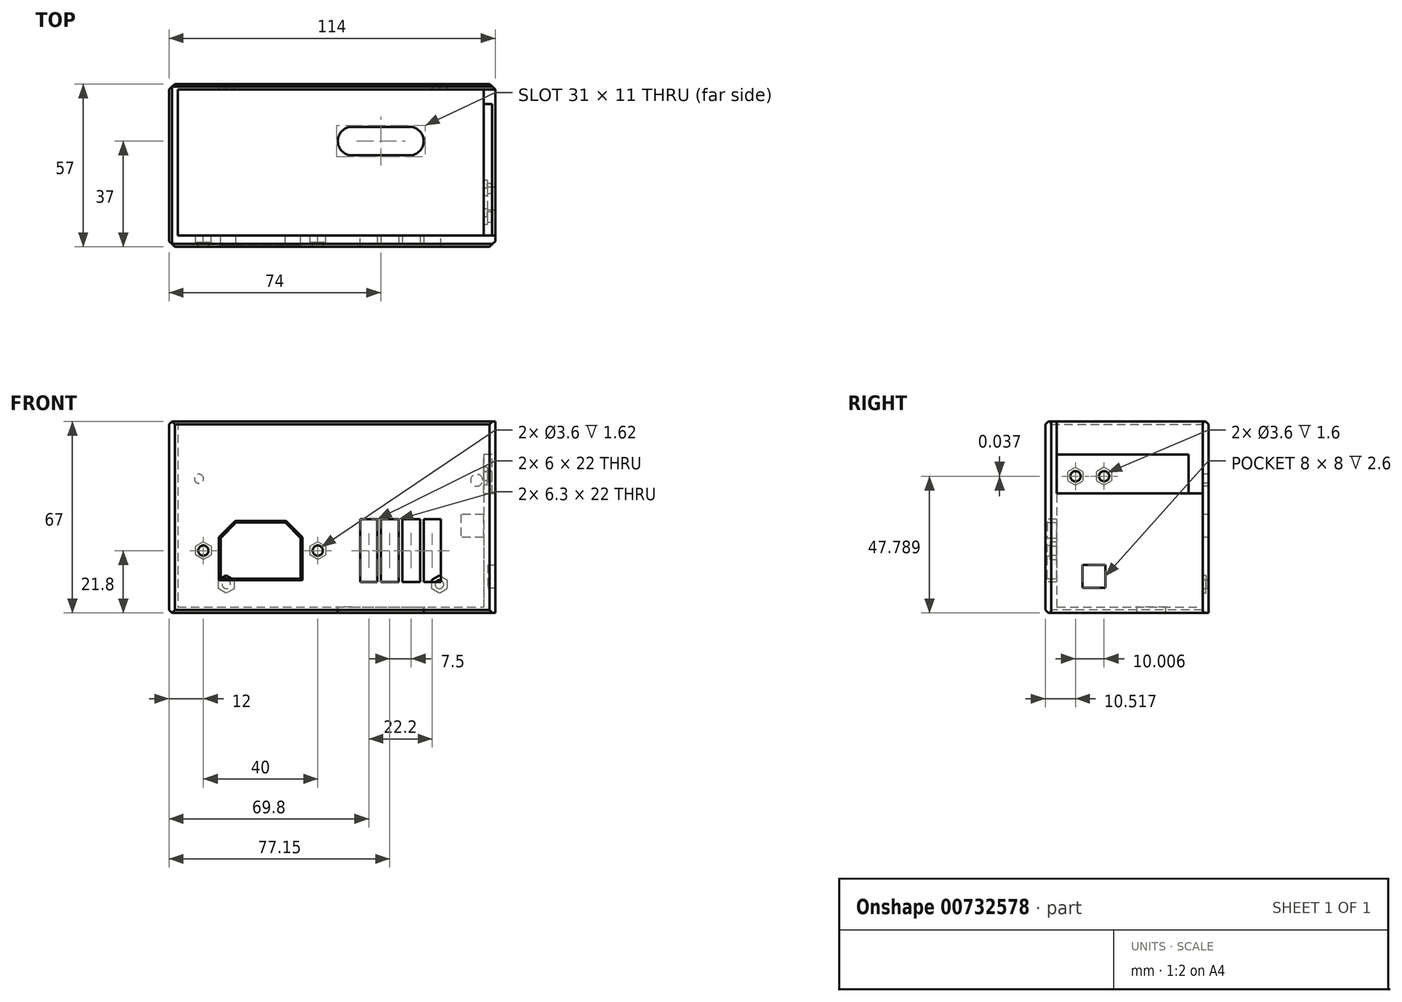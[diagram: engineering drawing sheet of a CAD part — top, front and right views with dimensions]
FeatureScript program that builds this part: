
annotation { "Feature Type Name" : "Feature", "Feature Type Description" : "" }
export const myFeature = defineFeature(function(context is Context, id is Id, definition is map)
    precondition{}
    {
        {
            var Q0;
            Q0=qCreatedBy(makeId("Front.planeOp"),FACE);
            cPlane(context, id + "F0", {"entities" : qUnion([Q0]), "cplaneType" : CPlaneType.OFFSET, "offset" : 2 * mm, "width" : 150 * mm, "height" : 150 * mm});
        }
        {
            var Q0;
            Q0=qCreatedBy(id+"F0.planeOp",FACE);
            var sketch = newSketch(context, id + "F1", { "sketchPlane" : qUnion([Q0])});
            skLineSegment(sketch, "E0.bottom", {"start": v(-111, 105) * mm, "end": v(0, 105) * mm});
            skLineSegment(sketch, "E0.top", {"start": v(-111, 40) * mm, "end": v(0, 40) * mm});
            skLineSegment(sketch, "E0.left", {"start": v(-111, 105) * mm, "end": v(-111, 40) * mm});
            skLineSegment(sketch, "E0.right", {"start": v(0, 105) * mm, "end": v(0, 40) * mm});
            skCircle(sketch, "E1.MirrorC", {"center": v(-93.99, 48.01) * mm, "radius": 1.5 * mm});
            skCircle(sketch, "E2.MirrorC", {"center": v(-19.49, 47.99) * mm, "radius": 1.5 * mm});
            skCircle(sketch, "E3.MirrorC", {"center": v(-6.46, 84.41) * mm, "radius": 2.1 * mm});
            skCircle(sketch, "E4", {"center": v(-103.55, 84.94) * mm, "radius": 1.6 * mm});
            skLineSegment(sketch, "E5.bottom", {"start": v(-4, 72.5) * mm, "end": v(-12, 72.5) * mm});
            skLineSegment(sketch, "E5.top", {"start": v(-4, 64.5) * mm, "end": v(-12, 64.5) * mm});
            skLineSegment(sketch, "E5.left", {"start": v(-4, 72.5) * mm, "end": v(-4, 64.5) * mm});
            skLineSegment(sketch, "E5.right", {"start": v(-12, 72.5) * mm, "end": v(-12, 64.5) * mm});
            skSolve(sketch);
        }
        {
            var Q0;
            Q0=qCreatedBy(id+"F0.planeOp",FACE);
            cPlane(context, id + "F2", {"entities" : qUnion([Q0]), "cplaneType" : CPlaneType.OFFSET, "offset" : 51 * mm, "width" : 150 * mm, "height" : 150 * mm});
        }
        {
            var Q0;
            Q0=qCreatedBy(makeId("Right.planeOp"),FACE);
            cPlane(context, id + "F3", {"entities" : qUnion([Q0]), "cplaneType" : CPlaneType.OFFSET, "offset" : 111 * mm, "oppositeDirection" : true, "width" : 150 * mm, "height" : 150 * mm});
        }
        {
            var Q0;
            Q0=qCreatedBy(makeId("Top.planeOp"),FACE);
            cPlane(context, id + "F4", {"entities" : qUnion([Q0]), "cplaneType" : CPlaneType.OFFSET, "offset" : 40 * mm, "width" : 150 * mm, "height" : 150 * mm});
        }
        {
            var Q0;
            Q0=qCreatedBy(makeId("Right.planeOp"),FACE);
            var sketch = newSketch(context, id + "F5", { "sketchPlane" : qUnion([Q0])});
            skLineSegment(sketch, "E6.bottom", {"start": v(-57, 40) * mm, "end": v(0, 40) * mm});
            skLineSegment(sketch, "E6.top", {"start": v(-57, 93.4) * mm, "end": v(0, 93.4) * mm});
            skLineSegment(sketch, "E6.left", {"start": v(-57, 40) * mm, "end": v(-57, 93.4) * mm});
            skLineSegment(sketch, "E6.right", {"start": v(0, 40) * mm, "end": v(0, 93.4) * mm});
            skCircle(sketch, "E7", {"center": v(-46.48, 85.79) * mm, "radius": 1.8 * mm});
            skCircle(sketch, "E8", {"center": v(-36.48, 85.83) * mm, "radius": 1.8 * mm});
            skLineSegment(sketch, "E9", {"start": v(0, 122) * mm, "end": v(0, -14.27) * mm, "construction": true});
            skSolve(sketch);
        }
        {
            var Q0;
            Q0=qCreatedBy(id+"F4.planeOp",FACE);
            var sketch = newSketch(context, id + "F6", { "sketchPlane" : qUnion([Q0])});
            skLineSegment(sketch, "E10.bottom", {"start": v(0, 0) * mm, "end": v(-114, 0) * mm});
            skLineSegment(sketch, "E10.top", {"start": v(0, -57) * mm, "end": v(-114, -57) * mm});
            skLineSegment(sketch, "E10.left", {"start": v(0, 0) * mm, "end": v(0, -57) * mm});
            skLineSegment(sketch, "E10.right", {"start": v(-114, 0) * mm, "end": v(-114, -57) * mm});
            skLineSegment(sketch, "E11.bottom", {"start": v(-55, -15) * mm, "end": v(-25, -15) * mm});
            skLineSegment(sketch, "E11.top", {"start": v(-55, -25) * mm, "end": v(-25, -25) * mm});
            skLineSegment(sketch, "E11.left", {"start": v(-55, -15) * mm, "end": v(-55, -25) * mm});
            skLineSegment(sketch, "E11.right", {"start": v(-25, -15) * mm, "end": v(-25, -25) * mm});
            skSolve(sketch);
        }
        {
            var Q0;
            Q0=qCreatedBy(id+"F3.planeOp",FACE);
            var sketch = newSketch(context, id + "F7", { "sketchPlane" : qUnion([Q0])});
            skLineSegment(sketch, "E12.0.0", {"start": v(0, 105) * mm, "end": v(-57, 105) * mm});
            skLineSegment(sketch, "E12.0.1", {"start": v(-57, 105) * mm, "end": v(-57, 40) * mm});
            skLineSegment(sketch, "E12.0.2", {"start": v(-57, 40) * mm, "end": v(0, 40) * mm});
            skLineSegment(sketch, "E12.0.3", {"start": v(0, 40) * mm, "end": v(0, 105) * mm});
            skSolve(sketch);
        }
        {
            var Q0;
            Q0=qSketchRegion(id+"F7",true);
            extrude(context, id + "F8", {"entities" : qUnion([Q0]), "oppositeDirection" : true, "depth" : 3 * mm, "offsetDistance" : 25 * mm});
        }
        {
            var Q0;
            Q0=makeQuery(id+"F6.imprint","IMPRINT",FACE,{"disambiguationData":[TD([[makeQuery(id+"F6.imprint","IMPRINT",EDGE,{"derivedFrom":sQuery(id+"F6.wireOp",EDGE,"E10.bottom")}),1.0]])]});
            extrude(context, id + "F9", {"entities" : qUnion([Q0]), "operationType" : NewBodyOperationType.ADD, "oppositeDirection" : true, "depth" : 2 * mm, "offsetDistance" : 25 * mm});
        }
        {
            var Q0;
            Q0=makeQuery(id+"F9.opExtrude","SWEPT_EDGE",EDGE,{"disambiguationData":[OSD([sQuery(id+"F6.wireOp",EDGE,"E11.top"),sQuery(id+"F6.wireOp",EDGE,"E11.right")])]});
            var Q1;
            Q1=makeQuery(id+"F9.opExtrude","SWEPT_EDGE",EDGE,{"disambiguationData":[OSD([sQuery(id+"F6.wireOp",EDGE,"E11.top"),sQuery(id+"F6.wireOp",EDGE,"E11.left")])]});
            var Q2;
            Q2=makeQuery(id+"F9.opExtrude","SWEPT_EDGE",EDGE,{"disambiguationData":[OSD([sQuery(id+"F6.wireOp",EDGE,"E11.bottom"),sQuery(id+"F6.wireOp",EDGE,"E11.left")])]});
            var Q3;
            Q3=makeQuery(id+"F9.opExtrude","SWEPT_EDGE",EDGE,{"disambiguationData":[OSD([sQuery(id+"F6.wireOp",EDGE,"E11.bottom"),sQuery(id+"F6.wireOp",EDGE,"E11.right")])]});
            fillet(context, id + "F10", {"entities" : qUnion([Q0, Q1, Q2, Q3]), "radius" : 5 * mm, "tangentPropagation" : true, "allowEdgeOverflow" : false});
        }
        {
            var Q0;
            Q0=makeQuery(id+"F5.imprint","IMPRINT",FACE,{"disambiguationData":[TD([[makeQuery(id+"F5.imprint","IMPRINT",EDGE,{"derivedFrom":sQuery(id+"F5.wireOp",EDGE,"E6.bottom")}),1.0]])]});
            extrude(context, id + "F11", {"entities" : qUnion([Q0]), "operationType" : NewBodyOperationType.ADD, "oppositeDirection" : true, "depth" : 4 * mm, "offsetDistance" : 25 * mm});
        }
        {
            var Q0;
            Q0=makeQuery(id+"F5.imprint","IMPRINT",FACE,{"disambiguationData":[TD([[makeQuery(id+"F5.imprint","IMPRINT",EDGE,{"derivedFrom":sQuery(id+"F5.wireOp",EDGE,"E6.bottom")}),1.0]])]});
            var sketch = newSketch(context, id + "F12", { "sketchPlane" : qUnion([Q0])});
            skLineSegment(sketch, "E13.bottom", {"start": v(-53, 105) * mm, "end": v(-2, 105) * mm});
            skLineSegment(sketch, "E13.top", {"start": v(-53, 79.75) * mm, "end": v(-2, 79.75) * mm});
            skLineSegment(sketch, "E13.left", {"start": v(-53, 105) * mm, "end": v(-53, 79.75) * mm});
            skLineSegment(sketch, "E13.right", {"start": v(-2, 105) * mm, "end": v(-2, 79.75) * mm});
            skSolve(sketch);
        }
        {
            var Q0;
            Q0=qSketchRegion(id+"F12",true);
            extrude(context, id + "F13", {"entities" : qUnion([Q0]), "operationType" : NewBodyOperationType.REMOVE, "oppositeDirection" : true, "depth" : 1.1 * mm, "offsetDistance" : 25 * mm});
        }
        {
            var Q0;
            Q0=makeQuery(id+"F11.boolean.opBoolean","MERGE",FACE,{"derivedFrom":[makeQuery(id+"F9.opExtrude","SWEPT_FACE",FACE,{"disambiguationData":[OSD([sQuery(id+"F6.wireOp",EDGE,"E10.left")])]}),makeQuery(id+"F11.opExtrude","CAP_FACE",FACE,{"disambiguationData":[OSD([sQuery(id+"F5.wireOp",EDGE,"E6.bottom"),sQuery(id+"F5.wireOp",EDGE,"E6.top"),sQuery(id+"F5.wireOp",EDGE,"E6.left"),sQuery(id+"F5.wireOp",EDGE,"E6.right"),sQuery(id+"F5.wireOp",EDGE,"E7"),sQuery(id+"F5.wireOp",EDGE,"E8")])],"isStart":true})]});
            extrude(context, id + "F14", {"entities" : qUnion([Q0]), "operationType" : NewBodyOperationType.ADD, "oppositeDirection" : true, "depth" : 4 * mm, "offsetDistance" : 25 * mm});
        }
        {
            var Q0;
            Q0=makeQuery(id+"F5.imprint","IMPRINT",FACE,{"disambiguationData":[TD([[makeQuery(id+"F5.imprint","IMPRINT",EDGE,{"derivedFrom":sQuery(id+"F5.wireOp",EDGE,"E6.bottom")}),1.0]])]});
            var sketch = newSketch(context, id + "F15", { "sketchPlane" : qUnion([Q0])});
            skLineSegment(sketch, "E14.bottom", {"start": v(-2, 79.75) * mm, "end": v(-7, 79.75) * mm});
            skLineSegment(sketch, "E14.top", {"start": v(-2, 105) * mm, "end": v(-7, 105) * mm});
            skLineSegment(sketch, "E14.left", {"start": v(-2, 79.75) * mm, "end": v(-2, 105) * mm});
            skLineSegment(sketch, "E14.right", {"start": v(-7, 79.75) * mm, "end": v(-7, 105) * mm});
            skSolve(sketch);
        }
        {
            var Q0;
            Q0=qSketchRegion(id+"F15",true);
            extrude(context, id + "F16", {"entities" : qUnion([Q0]), "operationType" : NewBodyOperationType.REMOVE, "oppositeDirection" : true, "depth" : 4.1 * mm, "offsetDistance" : 25 * mm});
        }
        {
            var Q0;
            Q0=qSketchRegion(id+"F1",true);
            extrude(context, id + "F17", {"entities" : qUnion([Q0]), "operationType" : NewBodyOperationType.ADD, "oppositeDirection" : true, "depth" : 2 * mm, "offsetDistance" : 25 * mm});
        }
        {
            var Q0;
            Q0=qCreatedBy(id+"F2.planeOp",FACE);
            var sketch = newSketch(context, id + "F18", { "sketchPlane" : qUnion([Q0])});
            skLineSegment(sketch, "E15.bottom", {"start": v(-111, 105) * mm, "end": v(0, 105) * mm});
            skLineSegment(sketch, "E15.top", {"start": v(-111, 40) * mm, "end": v(0, 40) * mm});
            skLineSegment(sketch, "E15.left", {"start": v(-111, 105) * mm, "end": v(-111, 40) * mm});
            skLineSegment(sketch, "E15.right", {"start": v(0, 105) * mm, "end": v(0, 40) * mm});
            skLineSegment(sketch, "E16", {"start": v(-90.6, 69.6) * mm, "end": v(-73.4, 69.6) * mm});
            skLineSegment(sketch, "E17", {"start": v(-73.4, 69.6) * mm, "end": v(-68, 64.2) * mm});
            skLineSegment(sketch, "E18", {"start": v(-68, 64.2) * mm, "end": v(-68, 50) * mm});
            skLineSegment(sketch, "E19", {"start": v(-68, 50) * mm, "end": v(-96, 50) * mm});
            skLineSegment(sketch, "E20", {"start": v(-96, 50) * mm, "end": v(-96, 64.2) * mm});
            skLineSegment(sketch, "E21", {"start": v(-96, 64.2) * mm, "end": v(-90.6, 69.6) * mm});
            skLineSegment(sketch, "E22", {"start": v(-82, 69.6) * mm, "end": v(-82, 50) * mm, "construction": true});
            skCircle(sketch, "E23", {"center": v(-62, 59.8) * mm, "radius": 1.8 * mm});
            skLineSegment(sketch, "E24", {"start": v(-82, 59.8) * mm, "end": v(-111, 59.8) * mm, "construction": true});
            skLineSegment(sketch, "E25", {"start": v(-111, 59.8) * mm, "end": v(-6.13, 59.8) * mm, "construction": true});
            skCircle(sketch, "E26", {"center": v(-102, 59.8) * mm, "radius": 1.8 * mm});
            skLineSegment(sketch, "E27.bottom", {"start": v(-47.2, 70.8) * mm, "end": v(-19, 70.8) * mm});
            skLineSegment(sketch, "E27.top", {"start": v(-47.2, 48.8) * mm, "end": v(-19, 48.8) * mm});
            skLineSegment(sketch, "E27.left", {"start": v(-47.2, 70.8) * mm, "end": v(-47.2, 48.8) * mm});
            skLineSegment(sketch, "E27.right", {"start": v(-19, 70.8) * mm, "end": v(-19, 48.8) * mm});
            skSolve(sketch);
        }
        {
            var Q0;
            Q0=makeQuery(id+"F11.boolean.opBoolean","MERGE",EDGE,{"derivedFrom":[makeQuery(id+"F9.opExtrude","SWEPT_EDGE",EDGE,{"disambiguationData":[OSD([sQuery(id+"F6.wireOp",EDGE,"E10.bottom"),sQuery(id+"F6.wireOp",EDGE,"E10.left")])]}),makeQuery(id+"F11.opExtrude","CAP_EDGE",EDGE,{"disambiguationData":[OSD([sQuery(id+"F5.wireOp",EDGE,"E6.right")])],"isStart":true})]});
            chamfer(context, id + "F19", {"entities" : qUnion([Q0]), "width" : 2 * mm, "tangentPropagation" : true});
        }
        {
            var Q0;
            Q0=makeQuery(id+"F9.boolean.opBoolean","MERGE",EDGE,{"derivedFrom":[makeQuery(id+"F8.opExtrude","CAP_EDGE",EDGE,{"disambiguationData":[OSD([sQuery(id+"F7.wireOp",EDGE,"E12.0.3")])],"isStart":false}),makeQuery(id+"F9.opExtrude","SWEPT_EDGE",EDGE,{"disambiguationData":[OSD([sQuery(id+"F6.wireOp",EDGE,"E10.bottom"),sQuery(id+"F6.wireOp",EDGE,"E10.right")])]})]});
            chamfer(context, id + "F20", {"entities" : qUnion([Q0]), "width" : 2 * mm, "tangentPropagation" : true});
        }
        {
            var Q0;
            Q0=makeQuery(id+"F18.imprint","IMPRINT",FACE,{"disambiguationData":[TD([[makeQuery(id+"F18.imprint","IMPRINT",EDGE,{"derivedFrom":sQuery(id+"F18.wireOp",EDGE,"E15.bottom")}),-1.0]])]});
            extrude(context, id + "F21", {"entities" : qUnion([Q0]), "operationType" : NewBodyOperationType.ADD, "depth" : 4 * mm, "offsetDistance" : 25 * mm});
        }
        {
            var Q0;
            Q0=makeQuery(id+"F11.boolean.opBoolean","MERGE",EDGE,{"derivedFrom":[makeQuery(id+"F9.opExtrude","SWEPT_EDGE",EDGE,{"disambiguationData":[OSD([sQuery(id+"F6.wireOp",EDGE,"E10.top"),sQuery(id+"F6.wireOp",EDGE,"E10.left")])]}),makeQuery(id+"F11.opExtrude","CAP_EDGE",EDGE,{"disambiguationData":[OSD([sQuery(id+"F5.wireOp",EDGE,"E6.left")])],"isStart":true})]});
            chamfer(context, id + "F22", {"entities" : qUnion([Q0]), "width" : 2 * mm, "tangentPropagation" : true});
        }
        {
            var Q0;
            Q0=makeQuery(id+"F9.boolean.opBoolean","MERGE",EDGE,{"derivedFrom":[makeQuery(id+"F8.opExtrude","CAP_EDGE",EDGE,{"disambiguationData":[OSD([sQuery(id+"F7.wireOp",EDGE,"E12.0.1")])],"isStart":false}),makeQuery(id+"F9.opExtrude","SWEPT_EDGE",EDGE,{"disambiguationData":[OSD([sQuery(id+"F6.wireOp",EDGE,"E10.top"),sQuery(id+"F6.wireOp",EDGE,"E10.right")])]})]});
            chamfer(context, id + "F23", {"entities" : qUnion([Q0]), "width" : 2 * mm, "tangentPropagation" : true});
        }
        {
            var Q0;
            Q0=makeQuery(id+"F21.boolean.opBoolean","MERGE",EDGE,{"derivedFrom":[makeQuery(id+"F8.opExtrude","SWEPT_EDGE",EDGE,{"disambiguationData":[OSD([sQuery(id+"F7.wireOp",EDGE,"E12.0.0"),sQuery(id+"F7.wireOp",EDGE,"E12.0.1")])]}),makeQuery(id+"F11.opExtrude","SWEPT_EDGE",EDGE,{"disambiguationData":[OSD([sQuery(id+"F5.wireOp",EDGE,"E6.top"),sQuery(id+"F5.wireOp",EDGE,"E6.left")])]}),makeQuery(id+"F21.opExtrude","CAP_EDGE",EDGE,{"disambiguationData":[OSD([sQuery(id+"F18.wireOp",EDGE,"E15.bottom")])],"isStart":false})]});
            var Q1;
            Q1=makeQuery(id+"F17.boolean.opBoolean","MERGE",EDGE,{"derivedFrom":[makeQuery(id+"F8.opExtrude","SWEPT_EDGE",EDGE,{"disambiguationData":[OSD([sQuery(id+"F7.wireOp",EDGE,"E12.0.0"),sQuery(id+"F7.wireOp",EDGE,"E12.0.3")])]}),makeQuery(id+"F11.opExtrude","SWEPT_EDGE",EDGE,{"disambiguationData":[OSD([sQuery(id+"F5.wireOp",EDGE,"E6.top"),sQuery(id+"F5.wireOp",EDGE,"E6.right")])]}),makeQuery(id+"F17.opExtrude","CAP_EDGE",EDGE,{"disambiguationData":[OSD([sQuery(id+"F1.wireOp",EDGE,"E0.bottom")])],"isStart":false})]});
            var Q2;
            Q2=makeQuery(id+"F8.opExtrude","CAP_EDGE",EDGE,{"disambiguationData":[OSD([sQuery(id+"F7.wireOp",EDGE,"E12.0.0")])],"isStart":false});
            chamfer(context, id + "F24", {"entities" : qUnion([Q0, Q1, Q2]), "width" : 1 * mm, "tangentPropagation" : true});
        }
        {
            var Q0;
            Q0=makeQuery(id+"F9.opExtrude","CAP_EDGE",EDGE,{"disambiguationData":[OSD([sQuery(id+"F6.wireOp",EDGE,"E10.top")])],"isStart":false});
            var Q1;
            Q1=makeQuery(id+"F9.opExtrude","CAP_EDGE",EDGE,{"disambiguationData":[OSD([sQuery(id+"F6.wireOp",EDGE,"E10.right")])],"isStart":false});
            chamfer(context, id + "F25", {"entities" : qUnion([Q0, Q1]), "width" : 1 * mm, "tangentPropagation" : true});
        }
        {
            var Q0;
            Q0=makeQuery(id+"F9.opExtrude","CAP_EDGE",EDGE,{"disambiguationData":[OSD([sQuery(id+"F6.wireOp",EDGE,"E11.top")])],"isStart":false});
            var Q1;
            {var subQ0=sQuery(id+"F6.wireOp",EDGE,"E11.left");var subQ1=sQuery(id+"F6.wireOp",EDGE,"E11.top");Q1=makeQuery(id+"F10.opFillet","BLEND_EDGE",EDGE,{"blendedFrom":[makeQuery(id+"F9.opExtrude","SWEPT_EDGE",EDGE,{"disambiguationData":[OSD([subQ1,subQ0])]}),makeQuery(id+"F9.opExtrude","CAP_FACE",FACE,{"disambiguationData":[OSD([sQuery(id+"F6.wireOp",EDGE,"E10.bottom"),sQuery(id+"F6.wireOp",EDGE,"E10.top"),sQuery(id+"F6.wireOp",EDGE,"E10.left"),sQuery(id+"F6.wireOp",EDGE,"E10.right"),sQuery(id+"F6.wireOp",EDGE,"E11.bottom"),subQ1,subQ0,sQuery(id+"F6.wireOp",EDGE,"E11.right")])],"isStart":false})],"blendedInto":[makeQuery(id+"F9.opExtrude","CAP_FACE",FACE,{"disambiguationData":[OSD([sQuery(id+"F6.wireOp",EDGE,"E10.bottom"),sQuery(id+"F6.wireOp",EDGE,"E10.top"),sQuery(id+"F6.wireOp",EDGE,"E10.left"),sQuery(id+"F6.wireOp",EDGE,"E10.right"),sQuery(id+"F6.wireOp",EDGE,"E11.bottom"),subQ1,subQ0,sQuery(id+"F6.wireOp",EDGE,"E11.right")])],"isStart":false})]});}
            var Q2;
            Q2=makeQuery(id+"F9.opExtrude","CAP_EDGE",EDGE,{"disambiguationData":[OSD([sQuery(id+"F6.wireOp",EDGE,"E11.bottom")])],"isStart":false});
            var Q3;
            {var subQ0=sQuery(id+"F6.wireOp",EDGE,"E11.right");var subQ1=sQuery(id+"F6.wireOp",EDGE,"E11.bottom");Q3=makeQuery(id+"F10.opFillet","BLEND_EDGE",EDGE,{"blendedFrom":[makeQuery(id+"F9.opExtrude","SWEPT_EDGE",EDGE,{"disambiguationData":[OSD([subQ1,subQ0])]}),makeQuery(id+"F9.opExtrude","CAP_FACE",FACE,{"disambiguationData":[OSD([sQuery(id+"F6.wireOp",EDGE,"E10.bottom"),sQuery(id+"F6.wireOp",EDGE,"E10.top"),sQuery(id+"F6.wireOp",EDGE,"E10.left"),sQuery(id+"F6.wireOp",EDGE,"E10.right"),subQ1,sQuery(id+"F6.wireOp",EDGE,"E11.top"),sQuery(id+"F6.wireOp",EDGE,"E11.left"),subQ0])],"isStart":false})],"blendedInto":[makeQuery(id+"F9.opExtrude","CAP_FACE",FACE,{"disambiguationData":[OSD([sQuery(id+"F6.wireOp",EDGE,"E10.bottom"),sQuery(id+"F6.wireOp",EDGE,"E10.top"),sQuery(id+"F6.wireOp",EDGE,"E10.left"),sQuery(id+"F6.wireOp",EDGE,"E10.right"),subQ1,sQuery(id+"F6.wireOp",EDGE,"E11.top"),sQuery(id+"F6.wireOp",EDGE,"E11.left"),subQ0])],"isStart":false})]});}
            var Q4;
            {var subQ0=sQuery(id+"F6.wireOp",EDGE,"E11.right");var subQ1=sQuery(id+"F6.wireOp",EDGE,"E11.bottom");Q4=makeQuery(id+"F10.opFillet","BLEND_EDGE",EDGE,{"blendedFrom":[makeQuery(id+"F9.opExtrude","SWEPT_EDGE",EDGE,{"disambiguationData":[OSD([subQ1,subQ0])]}),makeQuery(id+"F9.opExtrude","CAP_FACE",FACE,{"disambiguationData":[OSD([sQuery(id+"F6.wireOp",EDGE,"E10.bottom"),sQuery(id+"F6.wireOp",EDGE,"E10.top"),sQuery(id+"F6.wireOp",EDGE,"E10.left"),sQuery(id+"F6.wireOp",EDGE,"E10.right"),subQ1,sQuery(id+"F6.wireOp",EDGE,"E11.top"),sQuery(id+"F6.wireOp",EDGE,"E11.left"),subQ0])],"isStart":true})],"blendedInto":[makeQuery(id+"F9.opExtrude","CAP_FACE",FACE,{"disambiguationData":[OSD([sQuery(id+"F6.wireOp",EDGE,"E10.bottom"),sQuery(id+"F6.wireOp",EDGE,"E10.top"),sQuery(id+"F6.wireOp",EDGE,"E10.left"),sQuery(id+"F6.wireOp",EDGE,"E10.right"),subQ1,sQuery(id+"F6.wireOp",EDGE,"E11.top"),sQuery(id+"F6.wireOp",EDGE,"E11.left"),subQ0])],"isStart":true})]});}
            var Q5;
            {var subQ0=sQuery(id+"F6.wireOp",EDGE,"E11.left");var subQ1=sQuery(id+"F6.wireOp",EDGE,"E11.top");Q5=makeQuery(id+"F10.opFillet","BLEND_EDGE",EDGE,{"blendedFrom":[makeQuery(id+"F9.opExtrude","SWEPT_EDGE",EDGE,{"disambiguationData":[OSD([subQ1,subQ0])]}),makeQuery(id+"F9.opExtrude","CAP_FACE",FACE,{"disambiguationData":[OSD([sQuery(id+"F6.wireOp",EDGE,"E10.bottom"),sQuery(id+"F6.wireOp",EDGE,"E10.top"),sQuery(id+"F6.wireOp",EDGE,"E10.left"),sQuery(id+"F6.wireOp",EDGE,"E10.right"),sQuery(id+"F6.wireOp",EDGE,"E11.bottom"),subQ1,subQ0,sQuery(id+"F6.wireOp",EDGE,"E11.right")])],"isStart":true})],"blendedInto":[makeQuery(id+"F9.opExtrude","CAP_FACE",FACE,{"disambiguationData":[OSD([sQuery(id+"F6.wireOp",EDGE,"E10.bottom"),sQuery(id+"F6.wireOp",EDGE,"E10.top"),sQuery(id+"F6.wireOp",EDGE,"E10.left"),sQuery(id+"F6.wireOp",EDGE,"E10.right"),sQuery(id+"F6.wireOp",EDGE,"E11.bottom"),subQ1,subQ0,sQuery(id+"F6.wireOp",EDGE,"E11.right")])],"isStart":true})]});}
            fillet(context, id + "F26", {"entities" : qUnion([Q0, Q1, Q2, Q3, Q4, Q5]), "radius" : 0.5 * mm, "tangentPropagation" : true, "allowEdgeOverflow" : false});
        }
        {
            var Q0;
            Q0=makeQuery(id+"F21.opExtrude","SWEPT_FACE",FACE,{"disambiguationData":[OSD([sQuery(id+"F18.wireOp",EDGE,"E27.top")])]});
            var sketch = newSketch(context, id + "F27", { "sketchPlane" : qUnion([Q0])});
            skLineSegment(sketch, "E28.bottom", {"start": v(-33.7, -53) * mm, "end": v(-32.5, -53) * mm});
            skLineSegment(sketch, "E28.top", {"start": v(-33.7, -57) * mm, "end": v(-32.5, -57) * mm});
            skLineSegment(sketch, "E28.left", {"start": v(-33.7, -53) * mm, "end": v(-33.7, -57) * mm});
            skLineSegment(sketch, "E28.right", {"start": v(-32.5, -53) * mm, "end": v(-32.5, -57) * mm});
            skLineSegment(sketch, "E29", {"start": v(-33.1, -53) * mm, "end": v(-33.1, -57) * mm, "construction": true});
            skLineSegment(sketch, "E30.bottom", {"start": v(-41.2, -53) * mm, "end": v(-40, -53) * mm});
            skLineSegment(sketch, "E30.top", {"start": v(-41.2, -57) * mm, "end": v(-40, -57) * mm});
            skLineSegment(sketch, "E30.left", {"start": v(-41.2, -53) * mm, "end": v(-41.2, -57) * mm});
            skLineSegment(sketch, "E30.right", {"start": v(-40, -53) * mm, "end": v(-40, -57) * mm});
            skLineSegment(sketch, "E31.bottom", {"start": v(-26.2, -53) * mm, "end": v(-25, -53) * mm});
            skLineSegment(sketch, "E31.top", {"start": v(-26.2, -57) * mm, "end": v(-25, -57) * mm});
            skLineSegment(sketch, "E31.left", {"start": v(-26.2, -53) * mm, "end": v(-26.2, -57) * mm});
            skLineSegment(sketch, "E31.right", {"start": v(-25, -53) * mm, "end": v(-25, -57) * mm});
            skSolve(sketch);
        }
        {
            var Q0;
            Q0 = qSketchRegion(id + "F27", true);
            var Q1;
            Q1=makeQuery(id+"F21.opExtrude","SWEPT_FACE",FACE,{"disambiguationData":[OSD([sQuery(id+"F18.wireOp",EDGE,"E27.bottom")])]});
            extrude(context, id + "F28", {"entities" : qUnion([Q0]), "operationType" : NewBodyOperationType.ADD, "endBound" : BoundingType.UP_TO_SURFACE, "depth" : 25 * mm, "endBoundEntityFace" : qUnion([Q1]), "offsetDistance" : 25 * mm});
        }
        {
            var Q0;
            Q0=makeQuery(id+"F21.opExtrude","CAP_EDGE",EDGE,{"disambiguationData":[OSD([sQuery(id+"F18.wireOp",EDGE,"E19")])],"isStart":false});
            var Q1;
            Q1=makeQuery(id+"F21.opExtrude","CAP_EDGE",EDGE,{"disambiguationData":[OSD([sQuery(id+"F18.wireOp",EDGE,"E18")])],"isStart":false});
            var Q2;
            Q2=makeQuery(id+"F21.opExtrude","CAP_EDGE",EDGE,{"disambiguationData":[OSD([sQuery(id+"F18.wireOp",EDGE,"E17")])],"isStart":false});
            var Q3;
            Q3=makeQuery(id+"F21.opExtrude","CAP_EDGE",EDGE,{"disambiguationData":[OSD([sQuery(id+"F18.wireOp",EDGE,"E16")])],"isStart":false});
            var Q4;
            Q4=makeQuery(id+"F21.opExtrude","CAP_EDGE",EDGE,{"disambiguationData":[OSD([sQuery(id+"F18.wireOp",EDGE,"E21")])],"isStart":false});
            var Q5;
            Q5=makeQuery(id+"F21.opExtrude","CAP_EDGE",EDGE,{"disambiguationData":[OSD([sQuery(id+"F18.wireOp",EDGE,"E20")])],"isStart":false});
            chamfer(context, id + "F29", {"entities" : qUnion([Q0, Q1, Q2, Q3, Q4, Q5]), "width" : .6 * mm, "tangentPropagation" : true});
        }
        {
            var Q0;
            Q0=makeQuery(id+"F11.opExtrude","CAP_FACE",FACE,{"disambiguationData":[OSD([sQuery(id+"F5.wireOp",EDGE,"E6.bottom"),sQuery(id+"F5.wireOp",EDGE,"E6.top"),sQuery(id+"F5.wireOp",EDGE,"E6.left"),sQuery(id+"F5.wireOp",EDGE,"E6.right"),sQuery(id+"F5.wireOp",EDGE,"E7"),sQuery(id+"F5.wireOp",EDGE,"E8")])],"isStart":false});
            var sketch = newSketch(context, id + "F30", { "sketchPlane" : qUnion([Q0])});
            skCircle(sketch, "E32.cCircle", {"center": v(36.48, 85.83) * mm, "radius": 2.7 * mm, "construction": true});
            skLineSegment(sketch, "E32.0", {"start": v(39.18, 87.38) * mm, "end": v(39.18, 84.27) * mm});
            skLineSegment(sketch, "E32.1", {"start": v(39.18, 84.27) * mm, "end": v(36.48, 82.7) * mm});
            skLineSegment(sketch, "E32.2", {"start": v(36.48, 82.7) * mm, "end": v(33.78, 84.27) * mm});
            skLineSegment(sketch, "E32.3", {"start": v(33.78, 84.27) * mm, "end": v(33.78, 87.38) * mm});
            skLineSegment(sketch, "E32.4", {"start": v(33.78, 87.38) * mm, "end": v(36.48, 88.94) * mm});
            skLineSegment(sketch, "E32.5", {"start": v(36.48, 88.94) * mm, "end": v(39.18, 87.38) * mm});
            skPoint(sketch, "E32.0.midPoint", {"position": v(39.18, 85.83) * mm});
            skCircle(sketch, "E33.cCircle", {"center": v(46.48, 85.79) * mm, "radius": 2.7 * mm, "construction": true});
            skLineSegment(sketch, "E33.0", {"start": v(49.18, 87.35) * mm, "end": v(49.18, 84.23) * mm});
            skLineSegment(sketch, "E33.1", {"start": v(49.18, 84.23) * mm, "end": v(46.48, 82.67) * mm});
            skLineSegment(sketch, "E33.2", {"start": v(46.48, 82.67) * mm, "end": v(43.78, 84.23) * mm});
            skLineSegment(sketch, "E33.3", {"start": v(43.78, 84.23) * mm, "end": v(43.78, 87.35) * mm});
            skLineSegment(sketch, "E33.4", {"start": v(43.78, 87.35) * mm, "end": v(46.48, 88.9) * mm});
            skLineSegment(sketch, "E33.5", {"start": v(46.48, 88.9) * mm, "end": v(49.18, 87.35) * mm});
            skPoint(sketch, "E33.0.midPoint", {"position": v(49.18, 85.79) * mm});
            skSolve(sketch);
        }
        {
            var Q0;
            Q0 = qSketchRegion(id + "F30", true);
            extrude(context, id + "F31", {"entities" : qUnion([Q0]), "operationType" : NewBodyOperationType.REMOVE, "oppositeDirection" : true, "depth" : 1.3 * mm, "offsetDistance" : 25 * mm});
        }
        {
            var Q0;
            Q0=makeQuery(id+"F18.imprint","IMPRINT",FACE,{"disambiguationData":[TD([[makeQuery(id+"F18.imprint","IMPRINT",EDGE,{"derivedFrom":sQuery(id+"F18.wireOp",EDGE,"E15.bottom")}),-1.0]])]});
            var sketch = newSketch(context, id + "F32", { "sketchPlane" : qUnion([Q0])});
            skCircle(sketch, "E34.cCircle", {"center": v(-62, 59.8) * mm, "radius": 2.7 * mm, "construction": true});
            skLineSegment(sketch, "E34.0", {"start": v(-64.7, 58.24) * mm, "end": v(-64.7, 61.36) * mm});
            skLineSegment(sketch, "E34.1", {"start": v(-64.7, 61.36) * mm, "end": v(-62, 62.92) * mm});
            skLineSegment(sketch, "E34.2", {"start": v(-62, 62.92) * mm, "end": v(-59.3, 61.36) * mm});
            skLineSegment(sketch, "E34.3", {"start": v(-59.3, 61.36) * mm, "end": v(-59.3, 58.24) * mm});
            skLineSegment(sketch, "E34.4", {"start": v(-59.3, 58.24) * mm, "end": v(-62, 56.68) * mm});
            skLineSegment(sketch, "E34.5", {"start": v(-62, 56.68) * mm, "end": v(-64.7, 58.24) * mm});
            skPoint(sketch, "E34.0.midPoint", {"position": v(-64.7, 59.8) * mm});
            skCircle(sketch, "E35.cCircle", {"center": v(-102, 59.8) * mm, "radius": 2.7 * mm, "construction": true});
            skLineSegment(sketch, "E35.0", {"start": v(-104.7, 58.24) * mm, "end": v(-104.7, 61.36) * mm});
            skLineSegment(sketch, "E35.1", {"start": v(-104.7, 61.36) * mm, "end": v(-102, 62.92) * mm});
            skLineSegment(sketch, "E35.2", {"start": v(-102, 62.92) * mm, "end": v(-99.3, 61.36) * mm});
            skLineSegment(sketch, "E35.3", {"start": v(-99.3, 61.36) * mm, "end": v(-99.3, 58.24) * mm});
            skLineSegment(sketch, "E35.4", {"start": v(-99.3, 58.24) * mm, "end": v(-102, 56.68) * mm});
            skLineSegment(sketch, "E35.5", {"start": v(-102, 56.68) * mm, "end": v(-104.7, 58.24) * mm});
            skPoint(sketch, "E35.0.midPoint", {"position": v(-104.7, 59.8) * mm});
            skSolve(sketch);
        }
        {
            var Q0;
            Q0 = qSketchRegion(id + "F32", true);
            extrude(context, id + "F33", {"entities" : qUnion([Q0]), "operationType" : NewBodyOperationType.REMOVE, "depth" : 2.38 * mm, "offsetDistance" : 25 * mm});
        }
        {
            var Q0;
            Q0=makeQuery(id+"F1.imprint","IMPRINT",FACE,{"disambiguationData":[TD([[makeQuery(id+"F1.imprint","IMPRINT",EDGE,{"derivedFrom":sQuery(id+"F1.wireOp",EDGE,"E0.bottom")}),-1.0]])]});
            var sketch = newSketch(context, id + "F34", { "sketchPlane" : qUnion([Q0])});
            skCircle(sketch, "E36.cCircle", {"center": v(-93.99, 48.01) * mm, "radius": 2.7 * mm, "construction": true});
            skLineSegment(sketch, "E36.0", {"start": v(-91.29, 49.57) * mm, "end": v(-91.29, 46.45) * mm});
            skLineSegment(sketch, "E36.1", {"start": v(-91.29, 46.45) * mm, "end": v(-93.99, 44.9) * mm});
            skLineSegment(sketch, "E36.2", {"start": v(-93.99, 44.9) * mm, "end": v(-96.69, 46.45) * mm});
            skLineSegment(sketch, "E36.3", {"start": v(-96.69, 46.45) * mm, "end": v(-96.69, 49.57) * mm});
            skLineSegment(sketch, "E36.4", {"start": v(-96.69, 49.57) * mm, "end": v(-93.99, 51.13) * mm});
            skLineSegment(sketch, "E36.5", {"start": v(-93.99, 51.13) * mm, "end": v(-91.29, 49.57) * mm});
            skPoint(sketch, "E36.0.midPoint", {"position": v(-91.29, 48.01) * mm});
            skCircle(sketch, "E37.cCircle", {"center": v(-19.49, 47.99) * mm, "radius": 2.7 * mm, "construction": true});
            skLineSegment(sketch, "E37.0", {"start": v(-16.79, 49.55) * mm, "end": v(-16.79, 46.43) * mm});
            skLineSegment(sketch, "E37.1", {"start": v(-16.79, 46.43) * mm, "end": v(-19.49, 44.87) * mm});
            skLineSegment(sketch, "E37.2", {"start": v(-19.49, 44.87) * mm, "end": v(-22.19, 46.43) * mm});
            skLineSegment(sketch, "E37.3", {"start": v(-22.19, 46.43) * mm, "end": v(-22.19, 49.55) * mm});
            skLineSegment(sketch, "E37.4", {"start": v(-22.19, 49.55) * mm, "end": v(-19.49, 51.1) * mm});
            skLineSegment(sketch, "E37.5", {"start": v(-19.49, 51.1) * mm, "end": v(-16.79, 49.55) * mm});
            skPoint(sketch, "E37.0.midPoint", {"position": v(-16.79, 47.99) * mm});
            skSolve(sketch);
        }
        {
            var Q0;
            Q0 = qSketchRegion(id + "F34", true);
            extrude(context, id + "F35", {"entities" : qUnion([Q0]), "operationType" : NewBodyOperationType.REMOVE, "oppositeDirection" : true, "depth" : 1.2 * mm, "offsetDistance" : 25 * mm});
        }
        {
            var Q0;
            {var subQ1=sQuery(id+"F12.wireOp",EDGE,"E13.top");Q0=makeQuery(id+"F12.imprint","IMPRINT",FACE,{"disambiguationData":[TD([[makeQuery(id+"F12.imprint","IMPRINT",EDGE,{"derivedFrom":subQ1}),-1.0]])]});}
            var sketch = newSketch(context, id + "F36", { "sketchPlane" : qUnion([Q0])});
            skLineSegment(sketch, "E38.bottom", {"start": v(-44, 54.83) * mm, "end": v(-36, 54.83) * mm});
            skLineSegment(sketch, "E38.top", {"start": v(-44, 46.83) * mm, "end": v(-36, 46.83) * mm});
            skLineSegment(sketch, "E38.left", {"start": v(-44, 54.83) * mm, "end": v(-44, 46.83) * mm});
            skLineSegment(sketch, "E38.right", {"start": v(-36, 54.83) * mm, "end": v(-36, 46.83) * mm});
            skSolve(sketch);
        }
        {
            var Q0;
            Q0 = qSketchRegion(id + "F36", true);
            extrude(context, id + "F37", {"entities" : qUnion([Q0]), "operationType" : NewBodyOperationType.REMOVE, "oppositeDirection" : true, "depth" : 2.6 * mm, "offsetDistance" : 25 * mm});
        }
    });
